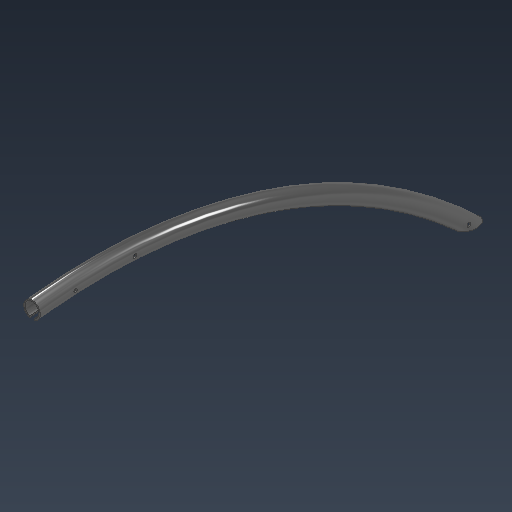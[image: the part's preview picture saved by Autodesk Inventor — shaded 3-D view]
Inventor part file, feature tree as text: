
AUTODESK INVENTOR PART (.ipt)
format: ipt  version: 2021 (Build 250183000, 183)  size: 318,464 bytes
history: native  units: mm
features: other x6, sketch x5, extrude x3, sweep x2, split x1, hole x1
ambient origin geometry x8: Origin, YZ Plane, XZ Plane, XY Plane, X Axis, Y Axis, Z Axis, Center Point
bodies: Solid1 (feature_tree)
feature tree (18):
  sketch  "Sketch1"  dims[d0=3300.0mm d1=1650.0mm]
  sweep  "Sweep1"
  sweep  "Sweep2"
  extrude  "Extrusion1"  Depth=43.0mm
  extrude  "Extrusion3"  Depth=1650.0mm
  other  "fea_loadSplit"
  split  "Split1"
  other  "midPlane"
  extrude  "Extrusion4"  Depth=6.0mm
  other  "tabHolePositioning"
  other  "midTabPlane"
  other  "projCentreAxis"
  other  "centreCut"
  hole  "tabHoles"  [1 undecoded]
  sketch  "Sketch2"  dims[d2=0.0mm d3=51.0mm]
  sketch  "Sketch3"  dims[d4=0.0mm d5=0.0mm d6=43.0mm]
  sketch  "Sketch4"  dims[d7=0.0mm d8=1650.0mm]
  sketch  "Sketch7"  dims[d9=0.0mm d10=0.0mm d11=1752.0mm d12=3402.0mm d13=1701.0mm d14=1200.0mm d15=1701.0mm d16=1701.0mm d17=200.0mm d18=51.0mm d19=0.0mm d22=14.0mm d23=0.0mm d24=-144.0mm d25=10.0mm d26=3300.0mm d27=100.0mm d28=0.0mm d34=3300.0mm d35=1200.0mm d36=1050.1mm d37=0.0mm d38=3300.0mm d39=1200.0mm d40=0.0mm d41=25.0mm d42=12.0mm d43=6.0mm d44=4.0mm d45=2.0mm d46=90.0deg d47=8.0mm d48=20.594885mm]
note: 1 required parameter value undecoded (feature->parameter linkage not recoverable at this tier; creation-order binding heuristic only, values carry confidence <= 0.55)
